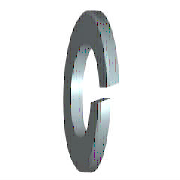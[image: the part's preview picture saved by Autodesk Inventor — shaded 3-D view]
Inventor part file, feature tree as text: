
AUTODESK INVENTOR PART (.ipt)
format: ipt  version: 2021 (Build 250183000, 183)  size: 126,976 bytes
history: native  units: mm (DEFAULTED — no unit token found)
features: sketch x2, extrude x1, other x1, plane x1
ambient origin geometry x6: Origin, YZ Plane, X Axis, Y Axis, Z Axis, Center Point
bodies: Solid1 (feature_tree), Body (feature_tree)
feature tree (5):
  extrude  "Cut"  Depth=21.1mm
  other  "Work Axis1"
  plane  "Work Plane1"
  sketch  "Sketch1"  dims[d0=12.2mm d1=21.1mm]
  sketch  "Sketch2"  dims[d2=2.65mm d3=0.0mm d4=0.53mm d5=0.53mm d6=12.217305mm d7=2.65mm d8=0.0mm d9=0.0mm d10=0.0mm d11=0.0mm d12=0.0mm]
